# Revit family: equip-faucet-elkay-lk943AFLC
name_source: partatom
category: Plumbing Fixtures
units: mm (PartAtom-declared; Revit-internal decimal feet)

## family parameters
Always vertical = Yes
Cut with Voids When Loaded = No
OmniClass Number = 23.45.55.17
OmniClass Title = Mixing Faucets
Part Type = Normal
Room Calculation Point = No
Round Connector Dimension = Use Radius
Shared = No
Work Plane-Based = Yes

## types (2) — shared parameters
Assembly Code = D2010900
CW Flow Rate = 2.2 GPM
Default Elevation = 4' - 0"
Description = Faucet
Faucet Material = Metal - Steel - Stainless - Chrome
HW Flow Rate = 2.2 GPM
L2 = Yes
Manufacturer = Elkay Manufacturing
MasterFormat Number = 22 42 39
22 42 39
22 42 39
MasterFormat Title = Commercial Faucets
Nominal Dia = 0' - 0 1/2"
Nominal Radius = 0' - 0 1/4"
OmniClass Code = 23.45.55.17
OmniClass Title = Mixing Faucets
Pre-Rinse Hose = Metal - Steel - Stainless - Chrome
Pre-Rinse Main = Metal - Steel - Stainless - Chrome
Pre-Rinse Sprayer = Metal - Steel - Stainless - Chrome
Specification URL = http://www.elkayusa.com
Stem Material = Metal - Steel
URL = www.elkayusa.com
zero-valued in all types: Cost

## per-type parameters (varying)
| type | AT08 | AT10 | HA08 N AT08 N TS08 | HA10 n AT10 |
| LK943AF08LC | Yes | No | Yes | No |
| LK943AF10LC | No | Yes | No | Yes |

note: column(s) folded — value = type name in every type: Model

## geometry (parser evidence)
native form markers: Sweep x2
no freeform markers — native parametric forms only
